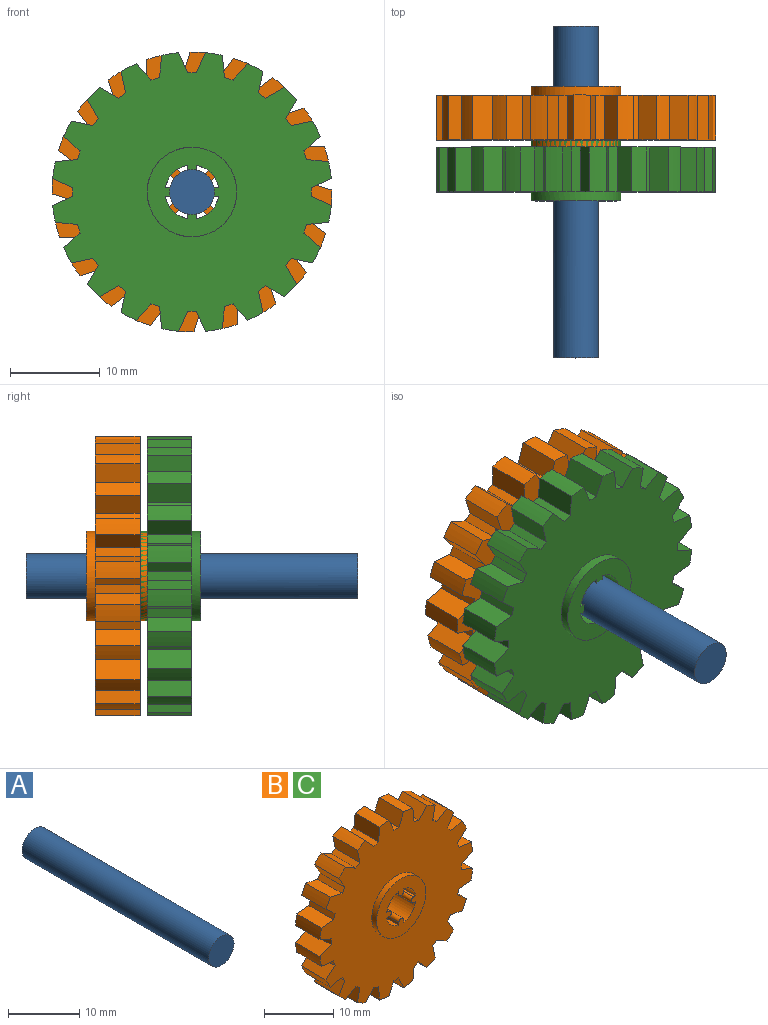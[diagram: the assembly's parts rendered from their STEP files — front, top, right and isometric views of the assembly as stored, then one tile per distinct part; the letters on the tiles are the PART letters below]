
ASSEMBLY  parts=3 mates=2
PART A: 3 faces, bbox 5x37x5 mm
  f0: plane 5x5mm, normal (0,1,0), area 19.6mm2, adj f1
  f1: cylinder r=2.5mm len=37mm, axis (0,-1,0), area 581.2mm2, adj f0,f2
  f2: plane 5x5mm, normal (0,-1,0), area 19.6mm2, adj f1
PART B: 102 faces, bbox 31.1x7x31.1 mm
  f0: plane 31.06x31.06mm, normal (0,1,0), area 593.1mm2, adj f1,f7,f8,f9,f10,f11,f12,f13
  f1: cylinder r=5mm len=10mm, axis (0,1,0), area 31.4mm2, adj f0,f2
  f2: plane 10x10mm, normal (0,1,0), area 53.8mm2, adj f1,f3,f87,f88,f89,f90,f91,f92
  f3: cylinder r=0.5mm len=7mm, axis (0,-1,0), area 11mm2, adj f2,f4,f87,f98
  f4: plane 10x10mm, normal (0,-1,0), area 53.8mm2, adj f3,f5,f87,f88,f89,f90,f91,f92
  f5: cylinder r=5mm len=10mm, axis (0,-1,0), area 31.4mm2, adj f4,f6
  f6: plane 31.06x31.06mm, normal (0,-1,0), area 593.1mm2, adj f5,f7,f8,f9,f10,f11,f12,f13
  f7: plane 5x0.95mm, normal (-0.31,0,0.95), area 5mm2, adj f0,f6,f8,f86
  f8: plane 5x2.45mm, normal (-0.99,0,0.1), area 12.3mm2, adj f0,f6,f7,f28
  f9: cylinder r=15.6mm len=5mm, axis (0,-1,0), area 9.5mm2, adj f0,f6,f29,f32
  f10: cylinder r=15.6mm len=5mm, axis (0,-1,0), area 9.5mm2, adj f0,f6,f31,f35
  f11: cylinder r=15.6mm len=5mm, axis (0,-1,0), area 9.5mm2, adj f0,f6,f37,f38
  f12: cylinder r=15.6mm len=5mm, axis (0,-1,0), area 9.5mm2, adj f0,f6,f40,f41
  f13: cylinder r=15.6mm len=5mm, axis (0,-1,0), area 9.5mm2, adj f0,f6,f43,f44
  f14: cylinder r=15.6mm len=5mm, axis (0,-1,0), area 9.5mm2, adj f0,f6,f46,f47
  f15: cylinder r=15.6mm len=5mm, axis (0,-1,0), area 9.5mm2, adj f0,f6,f49,f50
  f16: cylinder r=15.6mm len=5mm, axis (0,-1,0), area 9.5mm2, adj f0,f6,f52,f53
  f17: cylinder r=15.6mm len=5mm, axis (0,-1,0), area 9.5mm2, adj f0,f6,f55,f56
  f18: cylinder r=15.6mm len=5mm, axis (0,-1,0), area 9.5mm2, adj f0,f6,f58,f59
  f19: cylinder r=15.6mm len=5mm, axis (0,-1,0), area 9.5mm2, adj f0,f6,f61,f62
  f20: cylinder r=15.6mm len=5mm, axis (0,-1,0), area 9.5mm2, adj f0,f6,f64,f65
  f21: cylinder r=15.6mm len=5mm, axis (0,-1,0), area 9.5mm2, adj f0,f6,f67,f68
  f22: cylinder r=15.6mm len=5mm, axis (0,-1,0), area 9.5mm2, adj f0,f6,f70,f71
  f23: cylinder r=15.6mm len=5mm, axis (0,-1,0), area 9.5mm2, adj f0,f6,f73,f74
  f24: cylinder r=15.6mm len=5mm, axis (0,-1,0), area 9.5mm2, adj f0,f6,f76,f77
  f25: cylinder r=15.6mm len=5mm, axis (0,-1,0), area 9.5mm2, adj f0,f6,f79,f80
  f26: cylinder r=15.6mm len=5mm, axis (0,-1,0), area 9.5mm2, adj f0,f6,f82,f83
  f27: cylinder r=15.6mm len=5mm, axis (0,-1,0), area 9.5mm2, adj f0,f6,f85,f86
  f28: cylinder r=15.6mm len=5mm, axis (0,-1,0), area 9.5mm2, adj f0,f6,f8,f34
  f29: plane 5x2.45mm, normal (0.99,0,0.1), area 12.3mm2, adj f0,f6,f9,f30
  f30: plane 5x0.95mm, normal (0.31,0,0.95), area 5mm2, adj f0,f6,f29,f31
  f31: plane 5x1.83mm, normal (-0.74,0,0.67), area 12.3mm2, adj f0,f6,f10,f30
  f32: plane 5x2.25mm, normal (-0.91,0,0.41), area 12.3mm2, adj f0,f6,f9,f33
  f33: plane 5x1mm, normal (0,0,1), area 5mm2, adj f0,f6,f32,f34
  f34: plane 5x2.25mm, normal (0.91,0,0.41), area 12.3mm2, adj f0,f6,f28,f33
  f35: plane 5x2.41mm, normal (0.98,0,-0.21), area 12.3mm2, adj f0,f6,f10,f36
  f36: plane 5x0.81mm, normal (0.59,0,0.81), area 5mm2, adj f0,f6,f35,f37
  f37: plane 5x2.13mm, normal (-0.5,0,0.87), area 12.3mm2, adj f0,f6,f11,f36
  f38: plane 5x2.13mm, normal (0.87,0,-0.5), area 12.3mm2, adj f0,f6,f11,f39
  f39: plane 5x0.81mm, normal (0.81,0,0.59), area 5mm2, adj f0,f6,f38,f40
  f40: plane 5x2.41mm, normal (-0.21,0,0.98), area 12.3mm2, adj f0,f6,f12,f39
  f41: plane 5x1.83mm, normal (0.67,0,-0.74), area 12.3mm2, adj f0,f6,f12,f42
  f42: plane 5x0.95mm, normal (0.95,0,0.31), area 5mm2, adj f0,f6,f41,f43
  f43: plane 5x2.45mm, normal (0.1,0,0.99), area 12.3mm2, adj f0,f6,f13,f42
  f44: plane 5x2.25mm, normal (0.41,0,-0.91), area 12.3mm2, adj f0,f6,f13,f45
  f45: plane 5x1mm, normal (1,0,0), area 5mm2, adj f0,f6,f44,f46
  f46: plane 5x2.25mm, normal (0.41,0,0.91), area 12.3mm2, adj f0,f6,f14,f45
  f47: plane 5x2.45mm, normal (0.1,0,-0.99), area 12.3mm2, adj f0,f6,f14,f48
  f48: plane 5x0.95mm, normal (0.95,0,-0.31), area 5mm2, adj f0,f6,f47,f49
  f49: plane 5x1.83mm, normal (0.67,0,0.74), area 12.3mm2, adj f0,f6,f15,f48
  f50: plane 5x2.41mm, normal (-0.21,0,-0.98), area 12.3mm2, adj f0,f6,f15,f51
  f51: plane 5x0.81mm, normal (0.81,0,-0.59), area 5mm2, adj f0,f6,f50,f52
  f52: plane 5x2.13mm, normal (0.87,0,0.5), area 12.3mm2, adj f0,f6,f16,f51
  f53: plane 5x2.13mm, normal (-0.5,0,-0.87), area 12.3mm2, adj f0,f6,f16,f54
  f54: plane 5x0.81mm, normal (0.59,0,-0.81), area 5mm2, adj f0,f6,f53,f55
  f55: plane 5x2.41mm, normal (0.98,0,0.21), area 12.3mm2, adj f0,f6,f17,f54
  f56: plane 5x1.83mm, normal (-0.74,0,-0.67), area 12.3mm2, adj f0,f6,f17,f57
  f57: plane 5x0.95mm, normal (0.31,0,-0.95), area 5mm2, adj f0,f6,f56,f58
  f58: plane 5x2.45mm, normal (0.99,0,-0.1), area 12.3mm2, adj f0,f6,f18,f57
  f59: plane 5x2.25mm, normal (-0.91,0,-0.41), area 12.3mm2, adj f0,f6,f18,f60
  f60: plane 5x1mm, normal (0,0,-1), area 5mm2, adj f0,f6,f59,f61
  f61: plane 5x2.25mm, normal (0.91,0,-0.41), area 12.3mm2, adj f0,f6,f19,f60
  f62: plane 5x2.45mm, normal (-0.99,0,-0.1), area 12.3mm2, adj f0,f6,f19,f63
  f63: plane 5x0.95mm, normal (-0.31,0,-0.95), area 5mm2, adj f0,f6,f62,f64
  f64: plane 5x1.83mm, normal (0.74,0,-0.67), area 12.3mm2, adj f0,f6,f20,f63
  f65: plane 5x2.41mm, normal (-0.98,0,0.21), area 12.3mm2, adj f0,f6,f20,f66
  f66: plane 5x0.81mm, normal (-0.59,0,-0.81), area 5mm2, adj f0,f6,f65,f67
  f67: plane 5x2.13mm, normal (0.5,0,-0.87), area 12.3mm2, adj f0,f6,f21,f66
  f68: plane 5x2.13mm, normal (-0.87,0,0.5), area 12.3mm2, adj f0,f6,f21,f69
  f69: plane 5x0.81mm, normal (-0.81,0,-0.59), area 5mm2, adj f0,f6,f68,f70
  f70: plane 5x2.41mm, normal (0.21,0,-0.98), area 12.3mm2, adj f0,f6,f22,f69
  f71: plane 5x1.83mm, normal (-0.67,0,0.74), area 12.3mm2, adj f0,f6,f22,f72
  f72: plane 5x0.95mm, normal (-0.95,0,-0.31), area 5mm2, adj f0,f6,f71,f73
  f73: plane 5x2.45mm, normal (-0.1,0,-0.99), area 12.3mm2, adj f0,f6,f23,f72
  f74: plane 5x2.25mm, normal (-0.41,0,0.91), area 12.3mm2, adj f0,f6,f23,f75
  f75: plane 5x1mm, normal (-1,0,0), area 5mm2, adj f0,f6,f74,f76
  f76: plane 5x2.25mm, normal (-0.41,0,-0.91), area 12.3mm2, adj f0,f6,f24,f75
  f77: plane 5x2.45mm, normal (-0.1,0,0.99), area 12.3mm2, adj f0,f6,f24,f78
  f78: plane 5x0.95mm, normal (-0.95,0,0.31), area 5mm2, adj f0,f6,f77,f79
  f79: plane 5x1.83mm, normal (-0.67,0,-0.74), area 12.3mm2, adj f0,f6,f25,f78
  f80: plane 5x2.41mm, normal (0.21,0,0.98), area 12.3mm2, adj f0,f6,f25,f81
  f81: plane 5x0.81mm, normal (-0.81,0,0.59), area 5mm2, adj f0,f6,f80,f82
  f82: plane 5x2.13mm, normal (-0.87,0,-0.5), area 12.3mm2, adj f0,f6,f26,f81
  f83: plane 5x2.13mm, normal (0.5,0,0.87), area 12.3mm2, adj f0,f6,f26,f84
  f84: plane 5x0.81mm, normal (-0.59,0,0.81), area 5mm2, adj f0,f6,f83,f85
  f85: plane 5x2.41mm, normal (-0.98,0,-0.21), area 12.3mm2, adj f0,f6,f27,f84
  f86: plane 5x1.83mm, normal (0.74,0,0.67), area 12.3mm2, adj f0,f6,f7,f27
  f87: plane 7x0.46mm, normal (-1,0,0), area 3.2mm2, adj f2,f3,f4,f88
  f88: cylinder r=3mm len=7mm, axis (0,1,0), area 26mm2, adj f2,f4,f87,f92
  f89: cylinder r=3mm len=7mm, axis (0,1,0), area 26mm2, adj f2,f4,f95,f98
  f90: cylinder r=3mm len=7mm, axis (0,1,0), area 26mm2, adj f2,f4,f97,f99
  f91: cylinder r=3mm len=7mm, axis (0,1,0), area 26mm2, adj f2,f4,f94,f101
  f92: plane 7x0.46mm, normal (0,0,1), area 3.2mm2, adj f2,f4,f88,f93
  f93: cylinder r=0.5mm len=7mm, axis (0,-1,0), area 11mm2, adj f2,f4,f92,f94
  f94: plane 7x0.46mm, normal (0,0,-1), area 3.2mm2, adj f2,f4,f91,f93
  f95: plane 7x0.46mm, normal (0,0,1), area 3.2mm2, adj f2,f4,f89,f96
  f96: cylinder r=0.5mm len=7mm, axis (0,-1,0), area 11mm2, adj f2,f4,f95,f97
  f97: plane 7x0.46mm, normal (0,0,-1), area 3.2mm2, adj f2,f4,f90,f96
  f98: plane 7x0.46mm, normal (1,0,0), area 3.2mm2, adj f2,f3,f4,f89
  f99: plane 7x0.46mm, normal (1,0,0), area 3.2mm2, adj f2,f4,f90,f100
  f100: cylinder r=0.5mm len=7mm, axis (0,-1,0), area 11mm2, adj f2,f4,f99,f101
  f101: plane 7x0.46mm, normal (-1,0,0), area 3.2mm2, adj f2,f4,f91,f100
PART C: same geometry as B
PLACE A t=(-21.24,-1.35,-17.2)mm
PLACE B rot(axis=(0,1,0),47.7deg) t=(-21.24,-9.07,-17.2)mm
PLACE C t=(-21.24,-14.85,-17.2)mm
MATE cylindrical A.f1 <-> C.f1  axis (0,-1,0) through (-21.24,-19.85,-17.2)mm
MATE cylindrical C.f1 <-> B.f1  axis (0,-1,0) through (-21.24,-19.85,-17.2)mm
